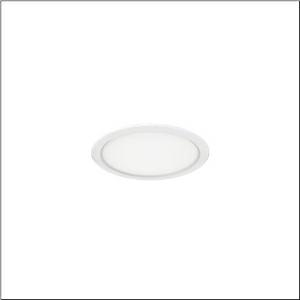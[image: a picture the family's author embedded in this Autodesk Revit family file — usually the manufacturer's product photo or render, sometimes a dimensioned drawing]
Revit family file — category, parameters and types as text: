
# Revit family: lunis_41_eco_51ds107d43b
name_source: partatom
category: Lighting Fixtures
units: mm (PartAtom-declared; Revit-internal decimal feet)

## family parameters
Cut with Voids When Loaded = No
Host = Face
Light Source = No
Part Type = Normal
Room Calculation Point = No
Round Connector Dimension = Use Diameter
Shared = No

## types (1)
- Lunis 41 Eco (1 x LED, 1580 lm, 12 W, 4000K)
    Apparent Load = 12 VA
    CIE Flux Codes = 47 80 97 100 100
    Color Rendering = 80
    Color Temperature = 4000K
    Default Elevation = 1800 mm
    Description = Lunis 41,  Eco, downlight, light emission: direct distribution, LED rated luminous flux: 1.580lm, light colour: 840, mains connection: 230V, AC, 50/60Hz, housing, round, of aluminium, coated, traffic white (RAL 9016), diameter: 166mm, recess depth: 54mm, protection rating (complete): IP20, protection rating (on room side): IP40, insulation class (complete): insulation class II (safety insulation), certification: CE, permissible ambient temperature for indoor applications: -20..+40°C, packaging unit: 1 piece
    Height = 0 mm  [stored 0 ft]
    Lamp = 1 x LED
    Lamp Light Flux = 1580 lm
    Lamp Power = 12 W
    Lamp count = 1
    Length = 166 mm
    Luminous efficacy = 132 lm/W
    Manufacturer = Siteco
    ModVariant = No
    Model = 51DS107D43B
    Mounting Place = Ceiling
    Mounting Type = Recessed
    Number of Poles = 1
    OnlyDefault = Yes
    Power Factor = 1
    Product Name = Lunis 41 Eco
    Product group = downlight
    ProductGroupID = 400
    Protection Class = Protection class II
    Protection Degree = IP 20
    RLX_Detail_Level = 1
    RLX_Emergency_Light_Flux = 0 lm
    RLX_Emergency_Type = 0
    RLX_Emergency_Type_DB = No
    RlxData = <blob elided: 8889 chars, md5=88faa2a9>
    Socket = socket
    Standby Power = 0 W
    System Light Flux = 1580 lm
    System Power = 12 W
    Type Comments = Product without accessories
    Type Image = l_1345912.jpg
    URL = http://relux.com
    VarID = ---
    Voltage = 0 V
    Weight = 0.00 kg
    Width = 0 mm  [stored 0 ft]

note: [stored X ft] marks values corroborated as IEEE doubles in the binary element streams (Revit-internal decimal feet)

## geometry (parser evidence)
native form markers: Sweep x8
no freeform markers — native parametric forms only
